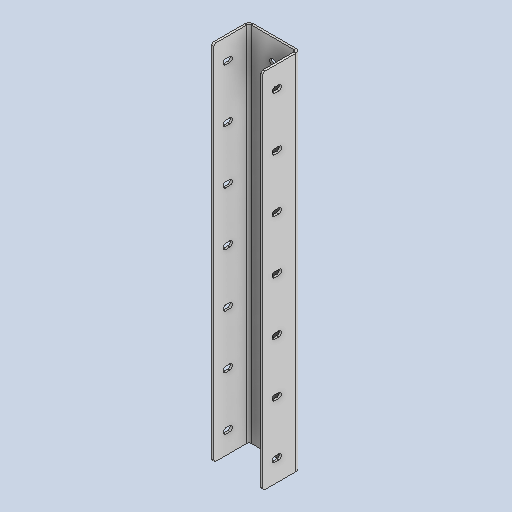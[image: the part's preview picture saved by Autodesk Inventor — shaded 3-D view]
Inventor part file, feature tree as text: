
AUTODESK INVENTOR PART (.ipt)
format: ipt  version: 2025 (Build 290162010, 162A)  size: 338,432 bytes
history: native  units: mm
features: sheet_metal_op x4, other x3, extrude x2, pattern_linear x1, fillet x1, sketch x1, projected_geometry x1
ambient origin geometry x8: Origin, YZ Plane, XZ Plane, XY Plane, X Axis, Y Axis, Z Axis, Center Point
bodies: Solid1 (feature_tree)
feature tree (13):
  sheet_metal_op  "Face1"
  sheet_metal_op  "Flange1"
  extrude  "Extrusion1"  Depth=340.0mm
  extrude  "Extrusion2"  Depth=2.0mm
  pattern_linear  "Rectangular Pattern2"  Spacing1=2.0mm  [1 undecoded]
  fillet  "Fillet1"  Radius=1.0mm
  other  "Plate1"
  sketch  "Sketch2"  dims[d0=44.0mm d1=340.0mm d2=2.0mm d3=2.0mm d4=1.0mm d5=4.0mm d6=2.0mm d7=35.0mm d8=90.0deg d9=2.0mm d10=8.0mm d11=2.0mm d12=2.0mm d13=5.0mm d14=13.0mm d15=20.0mm d16=0.0mm d17=0.0mm d21=5.0mm d22=20.0mm d23=0.0mm d24=0.0mm d25=70.0mm d27=50.0mm d28=4.0mm d29=2.5mm d30=1.0mm d31=5.0mm d32=2.0mm]
  other  "Plate2"
  sheet_metal_op  "Bend1"
  sheet_metal_op  "Corner1"
  projected_geometry  "Projected Loop1"
  other  "Definition1"
note: 1 required parameter value undecoded (feature->parameter linkage not recoverable at this tier; creation-order binding heuristic only, values carry confidence <= 0.55)
